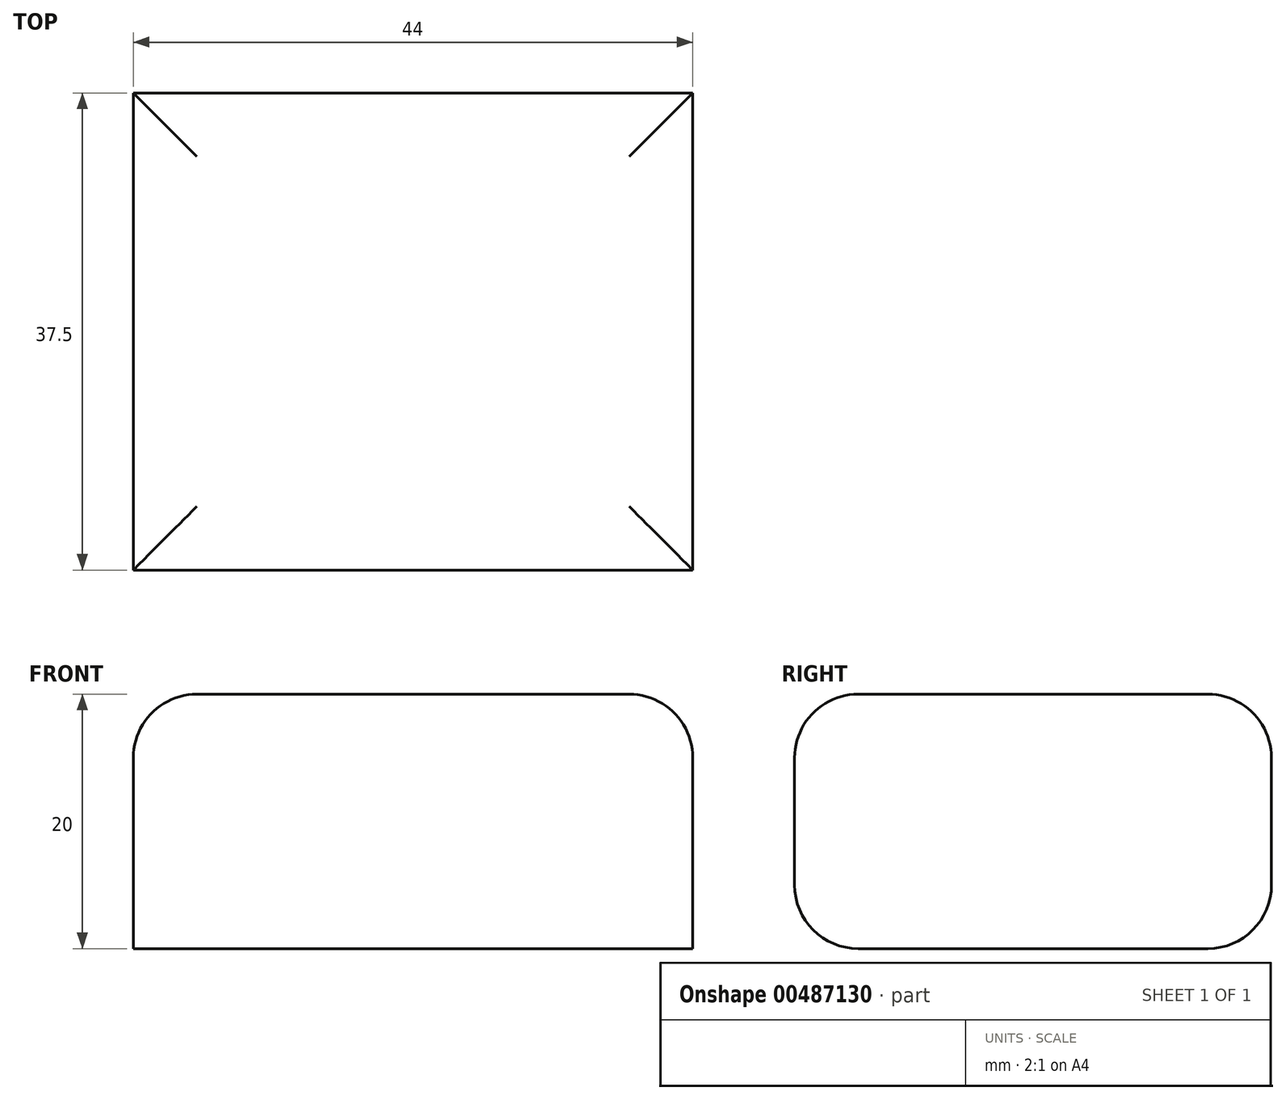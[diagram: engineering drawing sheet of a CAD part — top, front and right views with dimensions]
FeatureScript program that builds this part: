
annotation { "Feature Type Name" : "Feature", "Feature Type Description" : "" }
export const myFeature = defineFeature(function(context is Context, id is Id, definition is map)
    precondition{}
    {
        {
            var Q0;
            Q0=qCreatedBy(makeId("Front.planeOp"),FACE);
            var sketch = newSketch(context, id + "F0", { "sketchPlane" : qUnion([Q0])});
            skLineSegment(sketch, "E0.bottom", {"start": v(0, 0) * mm, "end": v(44, 0) * mm});
            skLineSegment(sketch, "E0.top", {"start": v(0, 20) * mm, "end": v(44, 20) * mm});
            skLineSegment(sketch, "E0.left", {"start": v(0, 0) * mm, "end": v(0, 20) * mm});
            skLineSegment(sketch, "E0.right", {"start": v(44, 0) * mm, "end": v(44, 20) * mm});
            skSolve(sketch);
        }
        {
            var Q0;
            Q0=makeQuery(id+"F0.imprint","IMPRINT",FACE,{"disambiguationData":[TD([[makeQuery(id+"F0.imprint","IMPRINT",EDGE,{"derivedFrom":sQuery(id+"F0.wireOp",EDGE,"E0.bottom")}),1.0]])]});
            extrude(context, id + "F1", {"entities" : qUnion([Q0]), "depth" : 37.5 * mm});
        }
        {
            var Q0;
            Q0=makeQuery(id+"F1.opExtrude","SWEPT_FACE",FACE,{"disambiguationData":[OSD([sQuery(id+"F0.wireOp",EDGE,"E0.top")])]});
            var Q1;
            Q1=makeQuery(id+"F1.opExtrude","CAP_EDGE",EDGE,{"disambiguationData":[OSD([sQuery(id+"F0.wireOp",EDGE,"E0.bottom")])],"isStart":false});
            var Q2;
            Q2=makeQuery(id+"F1.opExtrude","CAP_EDGE",EDGE,{"disambiguationData":[OSD([sQuery(id+"F0.wireOp",EDGE,"E0.bottom")])],"isStart":true});
            fillet(context, id + "F2", {"entities" : qUnion([Q0, Q1, Q2]), "radius" : 5 * mm, "tangentPropagation" : true, "allowEdgeOverflow" : false});
        }
        {
            var Q0;
            Q0=makeQuery(id+"F1.opExtrude","SWEPT_FACE",FACE,{"disambiguationData":[OSD([sQuery(id+"F0.wireOp",EDGE,"E0.right")])]});
            cPlane(context, id + "F3", {"entities" : qUnion([Q0]), "cplaneType" : CPlaneType.OFFSET, "offset" : 5 * mm, "oppositeDirection" : true, "width" : 150 * mm, "height" : 150 * mm});
        }
    });
